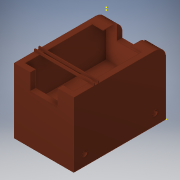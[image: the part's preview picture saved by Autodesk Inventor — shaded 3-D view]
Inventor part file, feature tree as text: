
AUTODESK INVENTOR PART (.ipt)
format: ipt  version: 2018 (Build 220112000, 112)  size: 249,856 bytes
history: native  units: mm
features: sketch x17, extrude x13, fillet x1
ambient origin geometry x8: Origin, YZ Plane, XZ Plane, XY Plane, X Axis, Y Axis, Z Axis, Center Point
bodies: Body1 (feature_tree), Body2 (feature_tree), Body3 (feature_tree)
feature tree (31):
  sketch  "Sketch10"  dims[d20=1100.0mm d21=1200.0mm]
  sketch  "Sketch11"  dims[d22=1700.0mm d23=0.0mm d24=1500.0mm]
  extrude  "Extrusion6"  Depth=1200.0mm
  extrude  "Extrusion7"  Depth=1500.0mm
  extrude  "Extrusion10"  Depth=100.0mm
  extrude  "Extrusion12"  Depth=1200.0mm TaperAngle=0.0deg
  extrude  "Extrusion13"  Depth=1500.0mm TaperAngle=0.0deg
  extrude  "Extrusion14"  Depth=10.0mm
  extrude  "Extrusion15"  Depth=1700.0mm TaperAngle=0.0deg
  extrude  "Extrusion16"  Depth=300.0mm
  sketch  "Sketch23"  dims[d63=60.0mm d64=40.0mm d65=0.0mm]
  sketch  "Sketch25"  dims[d77=100.0mm d78=80.0mm d79=600.0mm]
  extrude  "Extrusion17"  Depth=40.0mm TaperAngle=0.0deg
  extrude  "Extrusion18"  Depth=40.0mm TaperAngle=0.0deg
  extrude  "Extrusion19"  Depth=80.0mm
  sketch  "Sketch30"  dims[d86=10.0mm d87=0.0mm]
  fillet  "Fillet3"  Radius=600.0mm
  extrude  "Extrusion20"  Depth=100.0mm
  extrude  "Extrusion21"  Depth=600.0mm
  sketch  "Sketch12"  dims[d25=1000.0mm d26=0.0mm d34=100.0mm]
  sketch  "Sketch13"  dims[d35=100.0mm d36=1200.0mm d37=200.0mm d38=0.0mm d39=0.0mm]
  sketch  "Sketch16"  dims[d43=100.0mm d44=1500.0mm d45=0.0mm]
  sketch  "Sketch18"  dims[d46=900.0mm d47=10.0mm]
  sketch  "Sketch19"  dims[d48=1700.0mm d49=0.0mm d52=1700.0mm d53=0.0mm]
  sketch  "Sketch21"  dims[d58=510.0mm d59=300.0mm]
  sketch  "Sketch22"  dims[d60=100.0mm d61=40.0mm d62=0.0mm]
  sketch  "Sketch27"  dims[d81=20.0mm d82=100.0mm]
  sketch  "Sketch28"  dims[d83=80.0mm d84=600.0mm]
  sketch  "Sketch29"  dims[d85=20.0mm]
  sketch  "Sketch31"  dims[d90=250.676mm]
  sketch  "Sketch32"  dims[d91=10.0mm d92=0.0mm d93=250.676mm d94=10.0mm d95=0.0mm d96=200.0mm d97=10000.0mm d98=0.0mm d99=10000.0mm d100=0.0mm]
